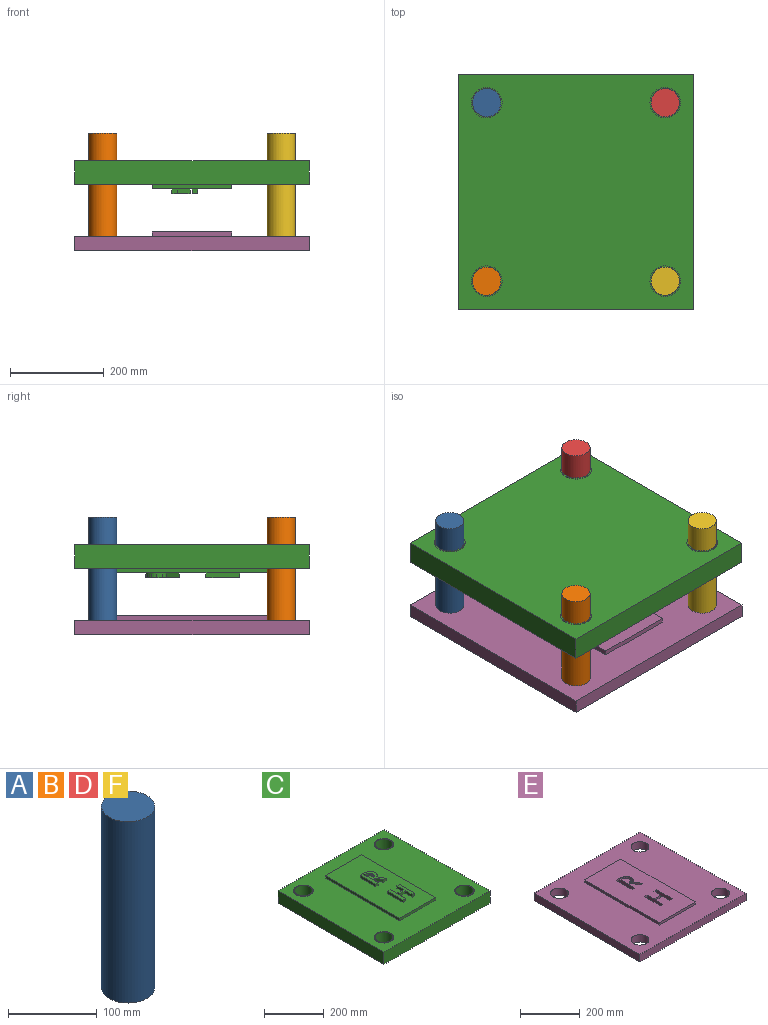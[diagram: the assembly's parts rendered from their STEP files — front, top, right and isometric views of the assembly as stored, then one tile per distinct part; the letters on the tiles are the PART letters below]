
ASSEMBLY  parts=6 mates=5
PART A: 3 faces, bbox 60x60x250 mm
  f0: cylinder r=30mm len=250mm, axis (0,0,-1), area 47123.9mm2, adj f1,f2
  f1: plane 60x60mm, normal (0,0,1), area 2827.4mm2, adj f0
  f2: plane 60x60mm, normal (0,0,-1), area 2827.4mm2, adj f0
PART B: same geometry as A
PART C: 76 faces, bbox 500x500x71 mm
  f0: plane 350x170mm, normal (0,0,1), area 55725mm2, adj f7,f8,f9,f10,f11,f12,f13,f14
  f1: plane 500x50mm, normal (0,1,0), area 25000mm2, adj f2,f4,f5,f6
  f2: plane 500x50mm, normal (-1,0,0), area 25000mm2, adj f1,f3,f5,f6
  f3: plane 500x50mm, normal (0,-1,0), area 25000mm2, adj f2,f4,f5,f6
  f4: plane 500x50mm, normal (1,0,0), area 25000mm2, adj f1,f3,f5,f6
  f5: plane 500x500mm, normal (0,0,1), area 177226.8mm2, adj f1,f2,f3,f4,f7,f8,f9,f10
  f6: plane 500x500mm, normal (0,0,-1), area 236726.8mm2, adj f1,f2,f3,f4,f56,f61,f66,f71
  f7: plane 350x10mm, normal (1,0,0), area 3500mm2, adj f0,f5,f8,f10
  f8: plane 170x10mm, normal (0,-1,0), area 1700mm2, adj f0,f5,f7,f9
  f9: plane 350x10mm, normal (-1,0,0), area 3500mm2, adj f0,f5,f8,f10
  f10: plane 170x10mm, normal (0,1,0), area 1700mm2, adj f0,f5,f7,f9
  f11: plane 11.75x10mm, normal (0,1,0), area 117.5mm2, adj f0,f12,f14,f15
  f12: plane 72.14x10mm, normal (-1,0,0), area 721.4mm2, adj f0,f11,f13,f15
  f13: plane 11.75x10mm, normal (0,-1,0), area 117.5mm2, adj f0,f12,f14,f15
  f14: plane 72.14x10mm, normal (1,0,0), area 721.4mm2, adj f0,f11,f13,f15
  f15: plane 72.14x11.75mm, normal (0,0,1), area 847.5mm2, adj f11,f12,f13,f14
  f16: plane 12.44x10mm, normal (0,-1,0), area 124.4mm2, adj f0,f17,f40,f41
  f17: plane 28.4x16.45mm, normal (0.87,0.5,0), area 328.2mm2, adj f0,f16,f18,f41
  f18: extruded ~10x9.78mm, area 129mm2, adj f0,f17,f19,f41
  f19: extruded ~13.31x10mm, area 140mm2, adj f0,f18,f20,f41
  f20: extruded ~10x9.36mm, area 97.1mm2, adj f0,f19,f21,f41
  f21: extruded ~10x7.1mm, area 92.1mm2, adj f0,f20,f22,f41
  f22: extruded ~10x8.08mm, area 92.6mm2, adj f0,f21,f23,f41
  f23: extruded ~10x9.09mm, area 92.5mm2, adj f0,f22,f24,f41
  f24: plane 10x5mm, normal (0,1,0), area 50mm2, adj f0,f23,f25,f41
  f25: plane 10x8.9mm, normal (-1,0,0), area 89mm2, adj f0,f24,f26,f41
  f26: plane 10x4.79mm, normal (0,-1,0), area 47.9mm2, adj f0,f25,f27,f41
  f27: extruded ~10x7.25mm, area 74.6mm2, adj f0,f26,f28,f41
  f28: extruded ~10x4.25mm, area 55.7mm2, adj f0,f27,f29,f41
  f29: extruded ~10x4.4mm, area 48.7mm2, adj f0,f28,f30,f41
  f30: extruded ~10x4.07mm, area 41.1mm2, adj f0,f29,f31,f41
  f31: extruded ~10x7.39mm, area 75mm2, adj f0,f30,f32,f41
  f32: extruded ~10x4.65mm, area 55mm2, adj f0,f31,f33,f41
  f33: extruded ~10x3.92mm, area 46.3mm2, adj f0,f32,f34,f41
  f34: extruded ~10x4.3mm, area 43.8mm2, adj f0,f33,f35,f41
  f35: plane 10x6.66mm, normal (0,1,0), area 66.6mm2, adj f0,f34,f36,f41
  f36: plane 10x8.61mm, normal (-1,0,0), area 86.1mm2, adj f0,f35,f37,f41
  f37: plane 10x5.48mm, normal (0,-1,0), area 54.8mm2, adj f0,f36,f38,f41
  f38: extruded ~10x1.03mm, area 10.3mm2, adj f0,f37,f39,f41
  f39: extruded ~10x0.63mm, area 6.4mm2, adj f0,f38,f40,f41
  f40: plane 26.14x13.61mm, normal (-0.89,-0.46,0), area 294.7mm2, adj f0,f16,f39,f41
  f41: plane 72.14x33.19mm, normal (0,0,1), area 1000.2mm2, adj f16,f17,f18,f19,f20,f21,f22,f23
  f42: plane 72.14x10mm, normal (1,0,0), area 721.4mm2, adj f0,f43,f49,f50
  f43: plane 11.75x10mm, normal (0,1,0), area 117.5mm2, adj f0,f42,f44,f50
  f44: plane 31.61x10mm, normal (-1,0,0), area 316.1mm2, adj f0,f43,f45,f50
  f45: plane 27.22x10mm, normal (0,1,0), area 272.2mm2, adj f0,f44,f46,f50
  f46: plane 10x8.04mm, normal (-1,0,0), area 80.4mm2, adj f0,f45,f47,f50
  f47: plane 27.22x10mm, normal (0,-1,0), area 272.2mm2, adj f0,f46,f48,f50
  f48: plane 32.5x10mm, normal (-1,0,0), area 325mm2, adj f0,f47,f49,f50
  f49: plane 11.75x10mm, normal (0,-1,0), area 117.5mm2, adj f0,f42,f48,f50
  f50: plane 72.14x38.97mm, normal (0,0,1), area 1066.2mm2, adj f42,f43,f44,f45,f46,f47,f48,f49
  f51: plane 11.94x10mm, normal (0,1,0), area 119.4mm2, adj f0,f52,f54,f55
  f52: plane 72.14x10mm, normal (-1,0,0), area 721.4mm2, adj f0,f51,f53,f55
  f53: plane 11.94x10mm, normal (0,-1,0), area 119.4mm2, adj f0,f52,f54,f55
  f54: plane 72.14x10mm, normal (1,0,0), area 721.4mm2, adj f0,f51,f53,f55
  f55: plane 72.14x11.94mm, normal (0,0,1), area 861.1mm2, adj f51,f52,f53,f54
  f56: cylinder r=32.5mm len=65mm, axis (0,0,-1), area 204.2mm2, adj f6,f60
  f57: cylinder r=30mm len=60mm, axis (0,0,-1), area 9801.8mm2, adj f59,f60
  f58: cylinder r=32.5mm len=65mm, axis (0,0,-1), area 204.2mm2, adj f5,f59
  f59: plane 65x65mm, normal (0,0,1), area 490.9mm2, adj f57,f58
  f60: plane 65x65mm, normal (0,0,-1), area 490.9mm2, adj f56,f57
  f61: cylinder r=32.5mm len=65mm, axis (0,0,-1), area 204.2mm2, adj f6,f65
  f62: cylinder r=30mm len=60mm, axis (0,0,-1), area 9801.8mm2, adj f64,f65
  f63: cylinder r=32.5mm len=65mm, axis (0,0,-1), area 204.2mm2, adj f5,f64
  f64: plane 65x65mm, normal (0,0,1), area 490.9mm2, adj f62,f63
  f65: plane 65x65mm, normal (0,0,-1), area 490.9mm2, adj f61,f62
  f66: cylinder r=32.5mm len=65mm, axis (0,0,-1), area 204.2mm2, adj f6,f70
  f67: cylinder r=30mm len=60mm, axis (0,0,-1), area 9801.8mm2, adj f69,f70
  f68: cylinder r=32.5mm len=65mm, axis (0,0,-1), area 204.2mm2, adj f5,f69
  f69: plane 65x65mm, normal (0,0,1), area 490.9mm2, adj f67,f68
  f70: plane 65x65mm, normal (0,0,-1), area 490.9mm2, adj f66,f67
  f71: cylinder r=32.5mm len=65mm, axis (0,0,-1), area 204.2mm2, adj f6,f75
  f72: cylinder r=30mm len=60mm, axis (0,0,-1), area 9801.8mm2, adj f74,f75
  f73: cylinder r=32.5mm len=65mm, axis (0,0,-1), area 204.2mm2, adj f5,f74
  f74: plane 65x65mm, normal (0,0,1), area 490.9mm2, adj f72,f73
  f75: plane 65x65mm, normal (0,0,-1), area 490.9mm2, adj f71,f72
PART D: same geometry as A
PART E: 56 faces, bbox 500x500x40 mm
  f0: plane 500x30mm, normal (0,1,0), area 15000mm2, adj f1,f7,f8,f9
  f1: plane 500x30mm, normal (-1,0,0), area 15000mm2, adj f0,f2,f8,f9
  f2: plane 500x30mm, normal (0,-1,0), area 15000mm2, adj f1,f7,f8,f9
  f3: cylinder r=30mm len=60mm, axis (0,0,-1), area 5654.9mm2, adj f8,f9
  f4: cylinder r=30mm len=60mm, axis (0,0,-1), area 5654.9mm2, adj f8,f9
  f5: cylinder r=30mm len=60mm, axis (0,0,-1), area 5654.9mm2, adj f8,f9
  f6: cylinder r=30mm len=60mm, axis (0,0,-1), area 5654.9mm2, adj f8,f9
  f7: plane 500x30mm, normal (1,0,0), area 15000mm2, adj f0,f2,f8,f9
  f8: plane 500x500mm, normal (0,0,1), area 179190.3mm2, adj f0,f1,f2,f3,f4,f5,f6,f7
  f9: plane 500x500mm, normal (0,0,-1), area 234650mm2, adj f0,f1,f2,f3,f4,f5,f6,f7
  f10: plane 170x10mm, normal (0,1,0), area 1700mm2, adj f8,f11,f54,f55
  f11: plane 350x10mm, normal (-1,0,0), area 3500mm2, adj f8,f10,f12,f55
  f12: plane 170x10mm, normal (0,-1,0), area 1700mm2, adj f8,f11,f54,f55
  f13: plane 74.64x40mm, normal (1,0,0), area 2985.4mm2, adj f9,f14,f50,f55
  f14: plane 40x12.35mm, normal (0,-1,0), area 493.9mm2, adj f9,f13,f15,f55
  f15: plane 74.64x40mm, normal (-1,0,0), area 2985.4mm2, adj f9,f14,f50,f55
  f16: plane 40x12.15mm, normal (0,-1,0), area 486.1mm2, adj f9,f17,f51,f55
  f17: plane 74.64x40mm, normal (-1,0,0), area 2985.4mm2, adj f9,f16,f18,f55
  f18: plane 40x12.15mm, normal (0,1,0), area 486.1mm2, adj f9,f17,f19,f55
  f19: plane 40x33.62mm, normal (1,0,0), area 1344.9mm2, adj f9,f18,f20,f55
  f20: plane 40x28.16mm, normal (0,1,0), area 1126.5mm2, adj f9,f19,f21,f55
  f21: plane 40x8.31mm, normal (1,0,0), area 332.5mm2, adj f9,f20,f22,f55
  f22: plane 40x28.16mm, normal (0,-1,0), area 1126.5mm2, adj f9,f21,f51,f55
  f23: plane 40x29.38mm, normal (-0.87,-0.5,0), area 1358mm2, adj f9,f24,f52,f55
  f24: plane 40x12.87mm, normal (0,1,0), area 514.6mm2, adj f9,f23,f25,f55
  f25: plane 40x27.04mm, normal (0.89,0.46,0), area 1219.6mm2, adj f9,f24,f26,f55
  f26: extruded ~40x0.66mm, area 26.3mm2, adj f9,f25,f27,f55
  f27: extruded ~40x1.06mm, area 42.5mm2, adj f9,f26,f28,f55
  f28: plane 40x5.67mm, normal (0,1,0), area 226.9mm2, adj f9,f27,f29,f55
  f29: plane 40x8.91mm, normal (1,0,0), area 356.5mm2, adj f9,f28,f30,f55
  f30: plane 40x6.89mm, normal (0,-1,0), area 275.5mm2, adj f9,f29,f31,f55
  f31: extruded ~40x4.45mm, area 181.3mm2, adj f9,f30,f32,f55
  f32: extruded ~40x4.05mm, area 191.5mm2, adj f9,f31,f33,f55
  f33: extruded ~40x4.81mm, area 227.6mm2, adj f9,f32,f34,f55
  f34: extruded ~40x7.64mm, area 310.4mm2, adj f9,f33,f35,f55
  f35: extruded ~40x4.21mm, area 170.1mm2, adj f9,f34,f36,f55
  f36: extruded ~40x4.55mm, area 201.6mm2, adj f9,f35,f37,f55
  f37: extruded ~40x4.4mm, area 230.7mm2, adj f9,f36,f38,f55
  f38: extruded ~40x7.5mm, area 308.7mm2, adj f9,f37,f39,f55
  f39: plane 40x4.96mm, normal (0,1,0), area 198.3mm2, adj f9,f38,f40,f55
  f40: plane 40x9.2mm, normal (1,0,0), area 368.2mm2, adj f9,f39,f41,f55
  f41: plane 40x5.17mm, normal (0,-1,0), area 206.8mm2, adj f9,f40,f42,f55
  f42: extruded ~40x9.41mm, area 382.7mm2, adj f9,f41,f43,f55
  f43: extruded ~40x8.36mm, area 383.1mm2, adj f9,f42,f44,f55
  f44: extruded ~40x7.34mm, area 381.2mm2, adj f9,f43,f45,f55
  f45: extruded ~40x9.68mm, area 401.9mm2, adj f9,f44,f46,f55
  f46: extruded ~40x13.77mm, area 579.4mm2, adj f9,f45,f52,f55
  f47: plane 74.64x40mm, normal (1,0,0), area 2985.4mm2, adj f9,f48,f53,f55
  f48: plane 40x12.15mm, normal (0,-1,0), area 486.1mm2, adj f9,f47,f49,f55
  f49: plane 74.64x40mm, normal (-1,0,0), area 2985.4mm2, adj f9,f48,f53,f55
  f50: plane 40x12.35mm, normal (0,1,0), area 493.9mm2, adj f9,f13,f15,f55
  f51: plane 40x32.7mm, normal (1,0,0), area 1308mm2, adj f9,f16,f22,f55
  f52: extruded ~40x10.12mm, area 533.7mm2, adj f9,f23,f46,f55
  f53: plane 40x12.15mm, normal (0,1,0), area 486.1mm2, adj f9,f47,f49,f55
  f54: plane 350x10mm, normal (1,0,0), area 3500mm2, adj f8,f10,f12,f55
  f55: plane 350x170mm, normal (0,0,1), area 55459.7mm2, adj f10,f11,f12,f13,f14,f15,f16,f17
PART F: same geometry as A
PLACE A t=(-68.48,206.59,-260.66)mm
PLACE B t=(-68.48,-173.41,-260.66)mm
PLACE C rot(axis=(0,-1,0),180deg) t=(107.27,3.24,-69.17)mm
PLACE D t=(311.52,206.59,-260.66)mm
PLACE E t=(135.76,3.24,-260.66)mm
PLACE F t=(311.52,-173.41,-260.66)mm
MATE fastened F.f0 <-> E.f6  axis (0,0,-1) through (311.52,-173.41,-260.66)mm
MATE slider C.f66 <-> F.f0  axis (0,0,1) through (311.52,-173.41,-69.17)mm
MATE fastened D.f0 <-> E.f4  axis (0,0,-1) through (311.52,206.59,-260.66)mm
MATE fastened B.f0 <-> E.f5  axis (0,0,-1) through (-68.48,-173.41,-260.66)mm
MATE fastened A.f0 <-> E.f3  axis (0,0,-1) through (-68.48,206.59,-260.66)mm
